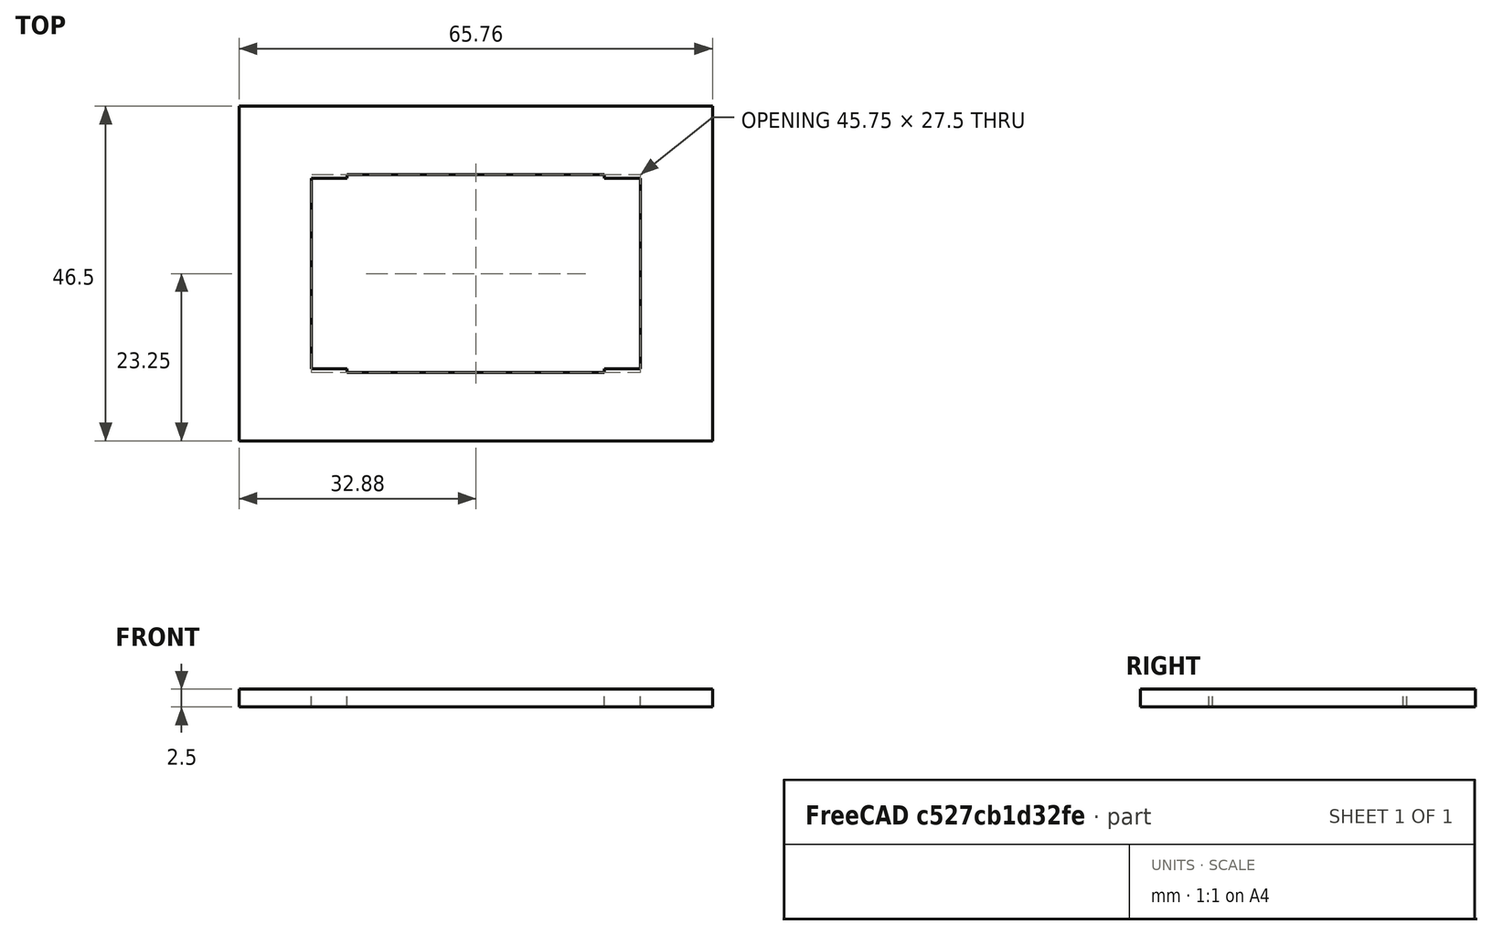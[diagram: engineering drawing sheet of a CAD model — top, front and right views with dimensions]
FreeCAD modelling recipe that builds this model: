
FCSTD DOCUMENT  (FreeCAD 0.19R24276 (Git))
Label: Test_VI_Meter_Cutout
License: All rights reserved
LicenseURL: http://en.wikipedia.org/wiki/All_rights_reserved
objects: Sketcher::SketchObject×1, PartDesign::Pad×1, PartDesign::Body×1
note: 4 computed .brp shape members not serialized (recipe doc carries the construction recipe); baked Part::Feature solids carry a one-line shape summary decoded from their .brp

FEATURE [Sketcher::SketchObject] Sketch
  FullyConstrained = true
  MapMode = 5
  Support = -> [XY_Plane]
  sketch-geometry (18):
    g0: LineSegment StartX=-22.875 StartY=13.25 StartZ=0 EndX=-17.875 EndY=13.25 EndZ=0
    g1: LineSegment StartX=22.875 StartY=13.25 StartZ=0 EndX=22.875 EndY=-13.25 EndZ=0
    g2: LineSegment StartX=22.875 StartY=-13.25 StartZ=0 EndX=17.875 EndY=-13.25 EndZ=0
    g3: LineSegment StartX=-22.875 StartY=-13.25 StartZ=0 EndX=-22.875 EndY=13.25 EndZ=0
    g4: LineSegment StartX=32.875 StartY=-23.25 StartZ=0 EndX=-32.875 EndY=-23.25 EndZ=0
    g5: LineSegment StartX=-32.875 StartY=-23.25 StartZ=0 EndX=-32.875 EndY=23.25 EndZ=0
    g6: LineSegment StartX=-32.875 StartY=23.25 StartZ=0 EndX=32.875 EndY=23.25 EndZ=0
    g7: LineSegment StartX=32.875 StartY=23.25 StartZ=0 EndX=32.875 EndY=-23.25 EndZ=0
    g8: LineSegment StartX=-22.875 StartY=13.25 StartZ=0 EndX=22.875 EndY=-13.25 EndZ=0
    g9: LineSegment StartX=-22.875 StartY=-13.25 StartZ=0 EndX=22.875 EndY=13.25 EndZ=0
    g10: LineSegment StartX=-17.875 StartY=13.25 StartZ=0 EndX=-17.875 EndY=13.75 EndZ=0
    g11: LineSegment StartX=-17.875 StartY=13.75 StartZ=0 EndX=17.875 EndY=13.75 EndZ=0
    g12: LineSegment StartX=17.875 StartY=13.75 StartZ=0 EndX=17.875 EndY=13.25 EndZ=0
    g13: LineSegment StartX=-17.875 StartY=-13.25 StartZ=0 EndX=-17.875 EndY=-13.75 EndZ=0
    g14: LineSegment StartX=-17.875 StartY=-13.75 StartZ=0 EndX=17.875 EndY=-13.75 EndZ=0
    g15: LineSegment StartX=17.875 StartY=-13.75 StartZ=0 EndX=17.875 EndY=-13.25 EndZ=0
    g16: LineSegment StartX=-17.875 StartY=-13.25 StartZ=0 EndX=-22.875 EndY=-13.25 EndZ=0
    g17: LineSegment StartX=17.875 StartY=13.25 StartZ=0 EndX=22.875 EndY=13.25 EndZ=0
  constraints (50):
    c: Coincident(g17,g1)
    c: Coincident(g1,g2)
    c: Coincident(g16,g3)
    c: Coincident(g3,g0)
    c: Horizontal(g0)
    c: Horizontal(g2)
    c: Vertical(g1)
    c: Vertical(g3)
    c: Coincident(g4,g5)
    c: Coincident(g5,g6)
    c: Coincident(g6,g7)
    c: Coincident(g7,g4)
    c: Horizontal(g4)
    c: Horizontal(g6)
    c: Vertical(g5)
    c: Vertical(g7)
    c: Coincident(g8,g0)
    c: Coincident(g8,g1)
    c: PointOnObject(g-1,g8)
    c: Coincident(g9,g16)
    c: Coincident(g9,g17)
    c: PointOnObject(g-1,g9)
    c: DistanceX(g5,g0) = 10
    c: DistanceY(g0,g5) = 10
    c: DistanceX(g1,g4) = 10
    c: DistanceY(g4,g1) = 10
    c: DistanceX(g0,g17) = 45.75
    c: DistanceY(g1,g1) = 26.5
    c: Vertical(g10)
    c: Coincident(g11,g10)
    c: Horizontal(g11)
    c: Coincident(g12,g11)
    c: Vertical(g12)
    c: Vertical(g13)
    c: Coincident(g14,g13)
    c: Horizontal(g14)
    c: Coincident(g15,g14)
    c: Vertical(g15)
    c: Coincident(g2,g15)
    c: Coincident(g16,g13)
    c: Tangent(g2,g16)
    c: Coincident(g0,g10)
    c: Coincident(g17,g12)
    c: Tangent(g0,g17)
    c: Equal(g0,g16)
    c: Equal(g16,g2)
    c: Equal(g2,g17)
    c: Equal(g10,g13)
    c: DistanceY(g10,g10) = 0.5
    c: DistanceX(g16,g16) = 5
FEATURE [PartDesign::Pad] Pad
  Direction = (1,1,1)
  Length = 2.5
  Length2 = 100
  Profile = -> Sketch
  Type = 0
FEATURE [PartDesign::Body] Body
  Group = -> [Sketch,Pad]
  Origin = -> Origin
  Tip = -> Pad
